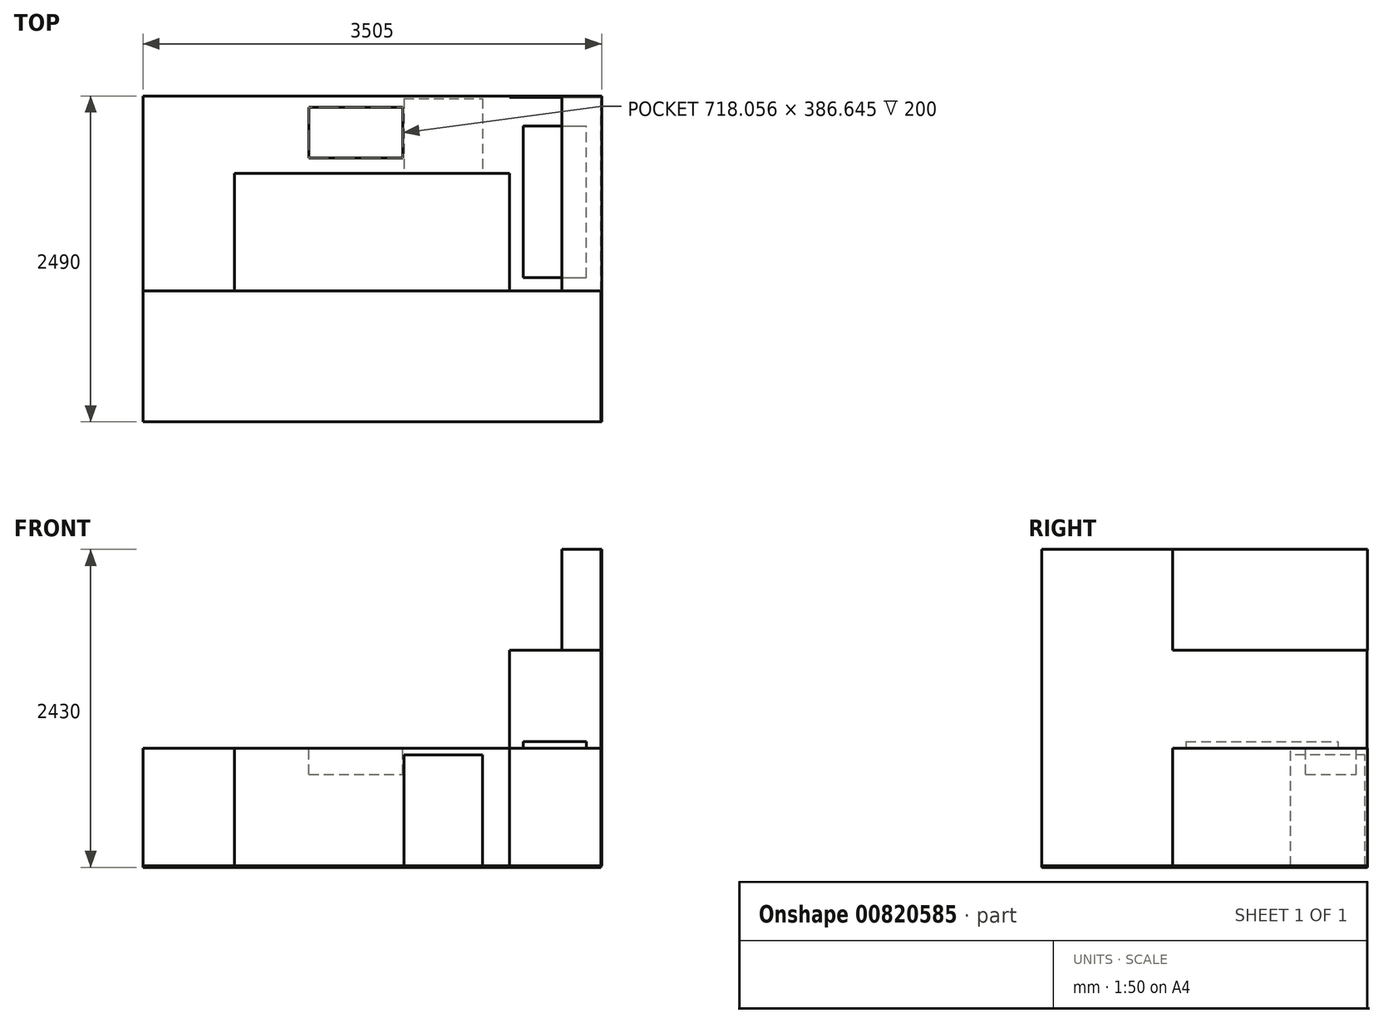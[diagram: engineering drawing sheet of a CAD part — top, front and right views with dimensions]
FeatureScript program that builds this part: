
annotation { "Feature Type Name" : "Feature", "Feature Type Description" : "" }
export const myFeature = defineFeature(function(context is Context, id is Id, definition is map)
    precondition{}
    {
        {
            var Q0;
            Q0=qCreatedBy(makeId("Top.planeOp"),FACE);
            var sketch = newSketch(context, id + "F0", { "sketchPlane" : qUnion([Q0])});
            skLineSegment(sketch, "E0.top", {"start": v(0, 590) * mm, "end": v(-3500, 590) * mm});
            skLineSegment(sketch, "E0.left", {"start": v(0, 0) * mm, "end": v(0, 590) * mm});
            skLineSegment(sketch, "E0.right", {"start": v(-3500, 0) * mm, "end": v(-3500, 590) * mm});
            skLineSegment(sketch, "E1.top", {"start": v(-3500, -900) * mm, "end": v(-2800, -900) * mm});
            skLineSegment(sketch, "E1.left", {"start": v(-3500, 0) * mm, "end": v(-3500, -900) * mm});
            skLineSegment(sketch, "E1.right", {"start": v(-2800, 0) * mm, "end": v(-2800, -900) * mm});
            skLineSegment(sketch, "E2.top", {"start": v(0, -900) * mm, "end": v(-700, -900) * mm});
            skLineSegment(sketch, "E2.left", {"start": v(0, 0) * mm, "end": v(0, -900) * mm});
            skLineSegment(sketch, "E2.right", {"start": v(-700, 0) * mm, "end": v(-700, -900) * mm});
            skLineSegment(sketch, "E3", {"start": v(-2800, 0) * mm, "end": v(-700, 0) * mm});
            skSolve(sketch);
        }
        {
            var Q0;
            Q0=makeQuery(id+"F0.imprint","IMPRINT",FACE,{"disambiguationData":[TD([[makeQuery(id+"F0.imprint","IMPRINT",EDGE,{"derivedFrom":sQuery(id+"F0.wireOp",EDGE,"E0.top")}),1.0]])]});
            extrude(context, id + "F1", {"entities" : qUnion([Q0]), "oppositeDirection" : true, "depth" : 900 * mm, "offsetDistance" : 25 * mm});
        }
        {
            var Q0;
            Q0=makeQuery(id+"F0.imprint","IMPRINT",FACE,{"disambiguationData":[TD([[makeQuery(id+"F0.imprint","IMPRINT",EDGE,{"derivedFrom":sQuery(id+"F0.wireOp",EDGE,"E0.top")}),1.0]])]});
            var sketch = newSketch(context, id + "F2", { "sketchPlane" : qUnion([Q0])});
            skLineSegment(sketch, "E4.bottom", {"start": v(-2648.98, 55.5) * mm, "end": v(-1008.98, 55.5) * mm});
            skLineSegment(sketch, "E4.top", {"start": v(-2648.98, 555.5) * mm, "end": v(-1008.98, 555.5) * mm});
            skLineSegment(sketch, "E4.left", {"start": v(-2648.98, 55.5) * mm, "end": v(-2648.98, 555.5) * mm});
            skLineSegment(sketch, "E4.right", {"start": v(-1008.98, 55.5) * mm, "end": v(-1008.98, 555.5) * mm});
            skLineSegment(sketch, "E5.bottom", {"start": v(-593, -797.57) * mm, "end": v(-113, -797.57) * mm});
            skLineSegment(sketch, "E5.top", {"start": v(-593, 362.43) * mm, "end": v(-113, 362.43) * mm});
            skLineSegment(sketch, "E5.left", {"start": v(-593, -797.57) * mm, "end": v(-593, 362.43) * mm});
            skLineSegment(sketch, "E5.right", {"start": v(-113, -797.57) * mm, "end": v(-113, 362.43) * mm});
            skLineSegment(sketch, "E6.bottom", {"start": v(-2231.65, 116.87) * mm, "end": v(-1513.59, 116.87) * mm});
            skLineSegment(sketch, "E6.top", {"start": v(-2231.65, 503.52) * mm, "end": v(-1513.59, 503.52) * mm});
            skLineSegment(sketch, "E6.left", {"start": v(-2231.65, 116.87) * mm, "end": v(-2231.65, 503.52) * mm});
            skLineSegment(sketch, "E6.right", {"start": v(-1513.59, 116.87) * mm, "end": v(-1513.59, 503.52) * mm});
            skSolve(sketch);
        }
        {
            var Q0;
            Q0=makeQuery(id+"F2.imprint","IMPRINT",FACE,{"disambiguationData":[TD([[makeQuery(id+"F2.imprint","IMPRINT",EDGE,{"derivedFrom":sQuery(id+"F2.wireOp",EDGE,"E6.bottom")}),1.0]])]});
            var Q1;
            Q1=sQuery(id+"F2.wireOp",EDGE,"E6.top");
            var Q2;
            Q2=sQuery(id+"F2.wireOp",EDGE,"E6.left");
            var Q3;
            Q3=sQuery(id+"F2.wireOp",EDGE,"E6.bottom");
            var Q4;
            Q4=sQuery(id+"F2.wireOp",EDGE,"E6.right");
            extrude(context, id + "F3", {"entities" : qUnion([Q0]), "operationType" : NewBodyOperationType.REMOVE, "surfaceEntities" : qUnion([Q1, Q2, Q3, Q4]), "oppositeDirection" : true, "depth" : 200 * mm, "offsetDistance" : 25 * mm});
        }
        {
            var Q0;
            Q0=makeQuery(id+"F2.imprint","IMPRINT",FACE,{"disambiguationData":[TD([[makeQuery(id+"F2.imprint","IMPRINT",EDGE,{"derivedFrom":sQuery(id+"F2.wireOp",EDGE,"E5.bottom")}),1.0]])]});
            extrude(context, id + "F4", {"entities" : qUnion([Q0]), "operationType" : NewBodyOperationType.ADD, "depth" : 50 * mm, "offsetDistance" : 25 * mm});
        }
        {
            var Q0;
            Q0=makeQuery(id+"F1.opExtrude","SWEPT_FACE",FACE,{"disambiguationData":[OSD([sQuery(id+"F0.wireOp",EDGE,"E3")])]});
            var sketch = newSketch(context, id + "F5", { "sketchPlane" : qUnion([Q0])});
            skLineSegment(sketch, "E7.bottom", {"start": v(-1505.54, -900) * mm, "end": v(-905.54, -900) * mm});
            skLineSegment(sketch, "E7.top", {"start": v(-1505.54, -50) * mm, "end": v(-905.54, -50) * mm});
            skLineSegment(sketch, "E7.left", {"start": v(-1505.54, -900) * mm, "end": v(-1505.54, -50) * mm});
            skLineSegment(sketch, "E7.right", {"start": v(-905.54, -900) * mm, "end": v(-905.54, -50) * mm});
            skSolve(sketch);
        }
        {
            var Q0;
            Q0=makeQuery(id+"F5.imprint","IMPRINT",FACE,{"disambiguationData":[TD([[makeQuery(id+"F5.imprint","IMPRINT",EDGE,{"derivedFrom":sQuery(id+"F5.wireOp",EDGE,"E7.bottom")}),1.0]])]});
            extrude(context, id + "F6", {"entities" : qUnion([Q0]), "operationType" : NewBodyOperationType.REMOVE, "oppositeDirection" : true, "depth" : 570 * mm, "offsetDistance" : 25 * mm});
        }
        {
            var Q0;
            Q0=qCreatedBy(makeId("Right.planeOp"),FACE);
            var sketch = newSketch(context, id + "F7", { "sketchPlane" : qUnion([Q0])});
            skLineSegment(sketch, "E8.bottom", {"start": v(-903.73, 0) * mm, "end": v(586.27, 0) * mm});
            skLineSegment(sketch, "E8.top", {"start": v(-903.73, 750) * mm, "end": v(586.27, 750) * mm});
            skLineSegment(sketch, "E8.left", {"start": v(-903.73, 0) * mm, "end": v(-903.73, 750) * mm});
            skLineSegment(sketch, "E8.right", {"start": v(586.27, 0) * mm, "end": v(586.27, 750) * mm});
            skSolve(sketch);
        }
        {
            var Q0;
            Q0=makeQuery(id+"F7.imprint","IMPRINT",FACE,{"disambiguationData":[TD([[makeQuery(id+"F7.imprint","IMPRINT",EDGE,{"derivedFrom":sQuery(id+"F7.wireOp",EDGE,"E8.bottom")}),1.0]])]});
            extrude(context, id + "F8", {"entities" : qUnion([Q0]), "depth" : 5 * mm, "offsetDistance" : 25 * mm});
        }
        {
            var Q0;
            Q0=makeQuery(id+"F8.opExtrude","CAP_FACE",FACE,{"disambiguationData":[OSD([sQuery(id+"F7.wireOp",EDGE,"E8.bottom"),sQuery(id+"F7.wireOp",EDGE,"E8.top"),sQuery(id+"F7.wireOp",EDGE,"E8.left"),sQuery(id+"F7.wireOp",EDGE,"E8.right")])],"isStart":true});
            var sketch = newSketch(context, id + "F9", { "sketchPlane" : qUnion([Q0])});
            skLineSegment(sketch, "E9.bottom", {"start": v(-586.27, 750) * mm, "end": v(-581.27, 750) * mm});
            skLineSegment(sketch, "E9.top", {"start": v(-586.27, 0) * mm, "end": v(-581.27, 0) * mm});
            skLineSegment(sketch, "E9.left", {"start": v(-586.27, 750) * mm, "end": v(-586.27, 0) * mm});
            skLineSegment(sketch, "E9.right", {"start": v(-581.27, 750) * mm, "end": v(-581.27, 0) * mm});
            skSolve(sketch);
        }
        {
            var Q0;
            Q0 = qSketchRegion(id + "F9", true);
            extrude(context, id + "F10", {"entities" : qUnion([Q0]), "depth" : 700 * mm, "offsetDistance" : 25 * mm});
        }
        {
            var Q0;
            Q0=makeQuery(id+"F1.opExtrude","SWEPT_FACE",FACE,{"disambiguationData":[OSD([sQuery(id+"F0.wireOp",EDGE,"E0.left"),sQuery(id+"F0.wireOp",EDGE,"E2.left")])]});
            var sketch = newSketch(context, id + "F11", { "sketchPlane" : qUnion([Q0])});
            skLineSegment(sketch, "E10.bottom", {"start": v(-900, -900) * mm, "end": v(-1900, -900) * mm});
            skLineSegment(sketch, "E10.top", {"start": v(-900, 1520) * mm, "end": v(-1900, 1520) * mm});
            skLineSegment(sketch, "E10.left", {"start": v(-900, -900) * mm, "end": v(-900, 1520) * mm});
            skLineSegment(sketch, "E10.right", {"start": v(-1900, -900) * mm, "end": v(-1900, 1520) * mm});
            skSolve(sketch);
        }
        {
            var Q0;
            Q0 = qSketchRegion(id + "F11", true);
            extrude(context, id + "F12", {"entities" : qUnion([Q0]), "operationType" : NewBodyOperationType.ADD, "depth" : 5 * mm, "offsetDistance" : 25 * mm});
        }
        {
            var Q0;
            Q0=makeQuery(id+"F12.boolean.opBoolean","MERGE",FACE,{"derivedFrom":[makeQuery(id+"F8.opExtrude","CAP_FACE",FACE,{"disambiguationData":[OSD([sQuery(id+"F7.wireOp",EDGE,"E8.bottom"),sQuery(id+"F7.wireOp",EDGE,"E8.top"),sQuery(id+"F7.wireOp",EDGE,"E8.left"),sQuery(id+"F7.wireOp",EDGE,"E8.right")])],"isStart":true}),makeQuery(id+"F12.opExtrude","CAP_FACE",FACE,{"disambiguationData":[OSD([sQuery(id+"F11.wireOp",EDGE,"E10.bottom"),sQuery(id+"F11.wireOp",EDGE,"E10.top"),sQuery(id+"F11.wireOp",EDGE,"E10.left"),sQuery(id+"F11.wireOp",EDGE,"E10.right")])],"isStart":true})]});
            var sketch = newSketch(context, id + "F13", { "sketchPlane" : qUnion([Q0])});
            skLineSegment(sketch, "E11.bottom", {"start": v(900, -900) * mm, "end": v(1900, -900) * mm});
            skLineSegment(sketch, "E11.top", {"start": v(900, -910) * mm, "end": v(1900, -910) * mm});
            skLineSegment(sketch, "E11.left", {"start": v(900, -900) * mm, "end": v(900, -910) * mm});
            skLineSegment(sketch, "E11.right", {"start": v(1900, -900) * mm, "end": v(1900, -910) * mm});
            skSolve(sketch);
        }
        {
            var Q0;
            Q0 = qSketchRegion(id + "F13", true);
            extrude(context, id + "F14", {"entities" : qUnion([Q0]), "depth" : 3500 * mm, "offsetDistance" : 25 * mm});
        }
        {
            var Q0;
            Q0=makeQuery(id+"F14.opExtrude","SWEPT_FACE",FACE,{"disambiguationData":[OSD([sQuery(id+"F13.wireOp",EDGE,"E11.left")])]});
            extrude(context, id + "F15", {"entities" : qUnion([Q0]), "depth" : 1490 * mm, "offsetDistance" : 25 * mm});
        }
        {
            var Q0;
            Q0=makeQuery(id+"F12.boolean.opBoolean","MERGE",FACE,{"derivedFrom":[makeQuery(id+"F8.opExtrude","CAP_FACE",FACE,{"disambiguationData":[OSD([sQuery(id+"F7.wireOp",EDGE,"E8.bottom"),sQuery(id+"F7.wireOp",EDGE,"E8.top"),sQuery(id+"F7.wireOp",EDGE,"E8.left"),sQuery(id+"F7.wireOp",EDGE,"E8.right")])],"isStart":false}),makeQuery(id+"F12.opExtrude","CAP_FACE",FACE,{"disambiguationData":[OSD([sQuery(id+"F11.wireOp",EDGE,"E10.bottom"),sQuery(id+"F11.wireOp",EDGE,"E10.top"),sQuery(id+"F11.wireOp",EDGE,"E10.left"),sQuery(id+"F11.wireOp",EDGE,"E10.right")])],"isStart":false})]});
            var sketch = newSketch(context, id + "F16", { "sketchPlane" : qUnion([Q0])});
            skLineSegment(sketch, "E12.bottom", {"start": v(-900, 750) * mm, "end": v(590, 750) * mm});
            skLineSegment(sketch, "E12.top", {"start": v(-900, 1520) * mm, "end": v(590, 1520) * mm});
            skLineSegment(sketch, "E12.left", {"start": v(-900, 750) * mm, "end": v(-900, 1520) * mm});
            skLineSegment(sketch, "E12.right", {"start": v(590, 750) * mm, "end": v(590, 1520) * mm});
            skSolve(sketch);
        }
        {
            var Q0;
            Q0 = qSketchRegion(id + "F16", true);
            extrude(context, id + "F17", {"entities" : qUnion([Q0]), "oppositeDirection" : true, "depth" : 305 * mm, "offsetDistance" : 25 * mm});
        }
    });
